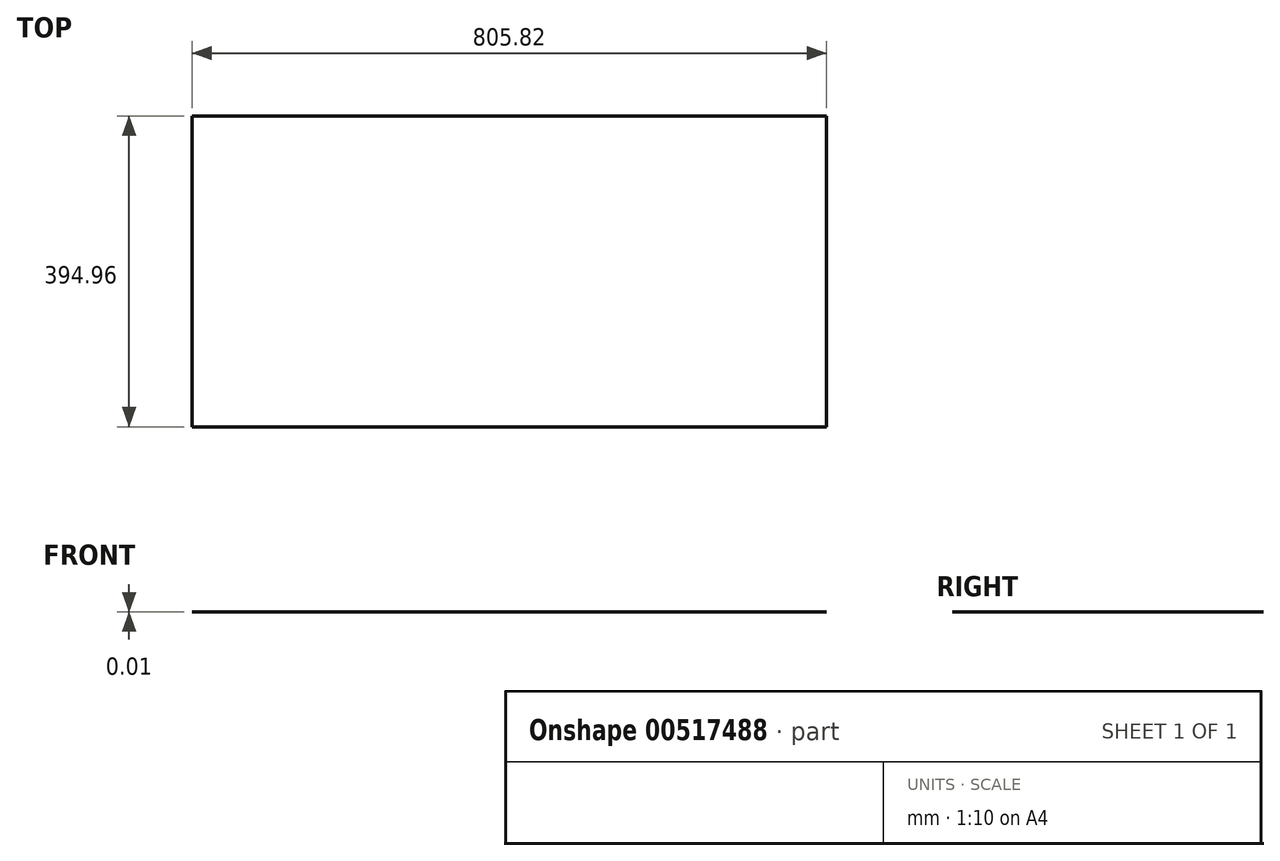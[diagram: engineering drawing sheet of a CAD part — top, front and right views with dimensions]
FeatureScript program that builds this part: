
annotation { "Feature Type Name" : "Feature", "Feature Type Description" : "" }
export const myFeature = defineFeature(function(context is Context, id is Id, definition is map)
    precondition{}
    {
        {
            var Q0;
            Q0=qCreatedBy(makeId("Top.planeOp"),FACE);
            var sketch = newSketch(context, id + "F0", { "sketchPlane" : qUnion([Q0])});
            skLineSegment(sketch, "E0.bottom", {"start": v(402.9, -197.48) * mm, "end": v(-402.9, -197.49) * mm});
            skLineSegment(sketch, "E0.top", {"start": v(402.9, 197.49) * mm, "end": v(-402.9, 197.48) * mm});
            skLineSegment(sketch, "E0.left", {"start": v(402.9, -197.48) * mm, "end": v(402.9, 197.49) * mm});
            skLineSegment(sketch, "E0.right", {"start": v(-402.9, -197.49) * mm, "end": v(-402.9, 197.48) * mm});
            skPoint(sketch, "E0.middle", {"position": v(0, 0) * mm});
            skSolve(sketch);
        }
        {
            var Q0;
            Q0=makeQuery(id+"F0.imprint","IMPRINT",FACE,{"disambiguationData":[TD([[makeQuery(id+"F0.imprint","IMPRINT",EDGE,{"derivedFrom":sQuery(id+"F0.wireOp",EDGE,"E0.bottom")}),-1.0]])]});
            extrude(context, id + "F1", {"entities" : qUnion([Q0]), "depth" : 3 / 406.4 * mm, "offsetDistance" : 25.4 * mm});
        }
    });
